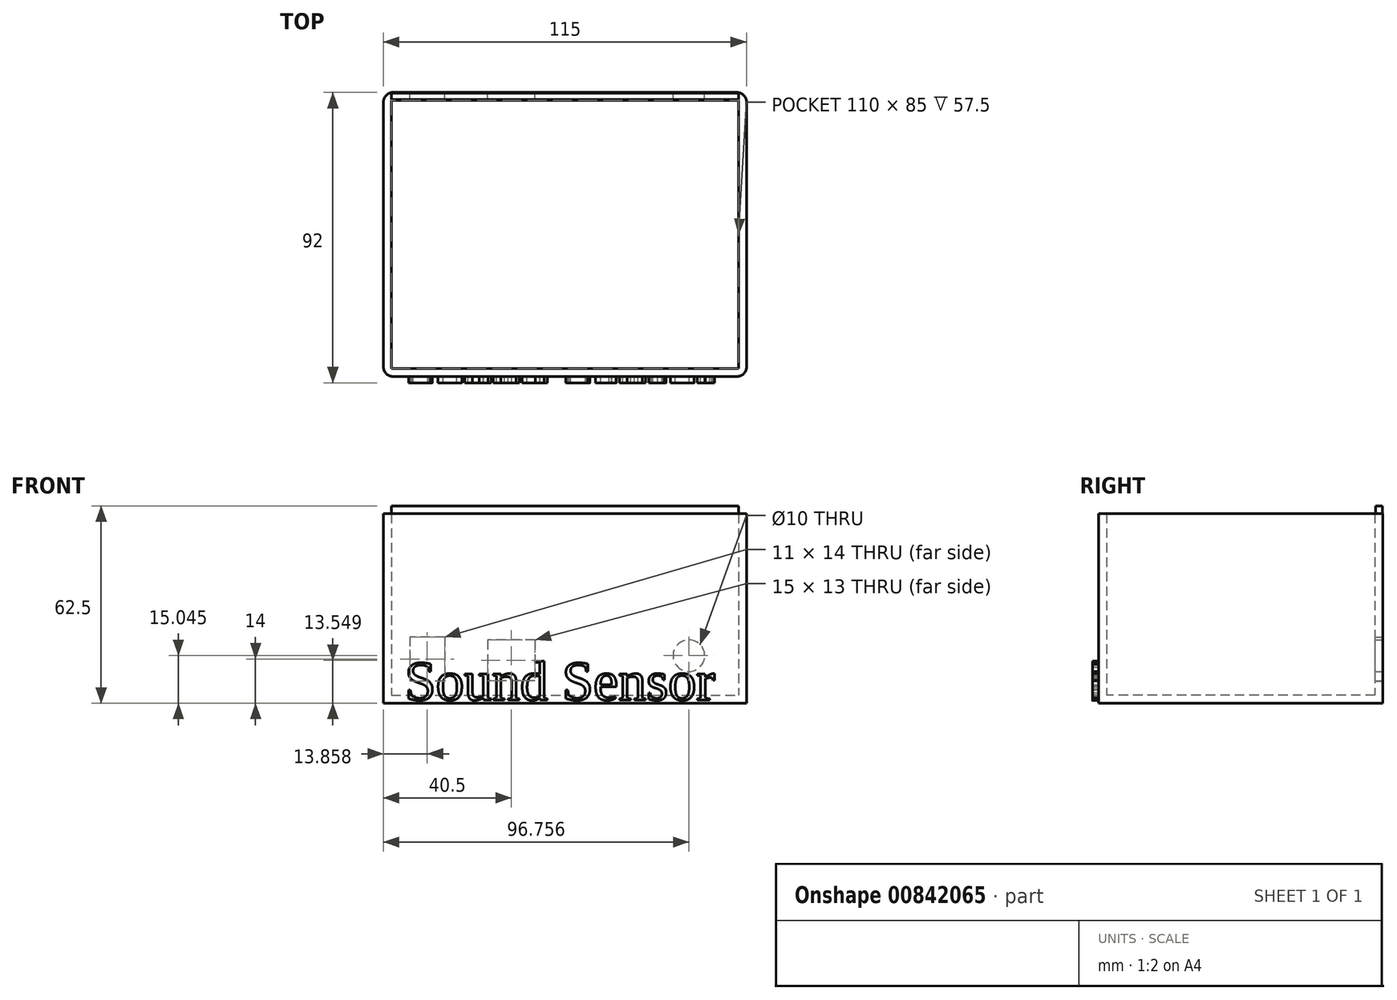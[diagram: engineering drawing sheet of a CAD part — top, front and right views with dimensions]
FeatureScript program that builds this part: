
annotation { "Feature Type Name" : "Feature", "Feature Type Description" : "" }
export const myFeature = defineFeature(function(context is Context, id is Id, definition is map)
    precondition{}
    {
        {
            var Q0;
            Q0=qCreatedBy(makeId("Top.planeOp"),FACE);
            var sketch = newSketch(context, id + "F0", { "sketchPlane" : qUnion([Q0])});
            skLineSegment(sketch, "E0.bottom", {"start": v(-57.5, 43.87) * mm, "end": v(57.5, 43.87) * mm});
            skLineSegment(sketch, "E0.top", {"start": v(-57.5, -46.13) * mm, "end": v(57.5, -46.13) * mm});
            skLineSegment(sketch, "E0.left", {"start": v(-57.5, 43.87) * mm, "end": v(-57.5, -46.13) * mm});
            skLineSegment(sketch, "E0.right", {"start": v(57.5, 43.87) * mm, "end": v(57.5, -46.13) * mm});
            skLineSegment(sketch, "E1", {"start": v(0, 29.34) * mm, "end": v(57.5, 29.34) * mm});
            skSolve(sketch);
        }
        {
            var Q0;
            Q0=qSketchRegion(id+"F0",true);
            extrude(context, id + "F1", {"entities" : qUnion([Q0]), "depth" : 60 * mm, "offsetDistance" : 25 * mm});
        }
        {
            var Q0;
            Q0=makeQuery(id+"F1.opExtrude","CAP_FACE",FACE,{"disambiguationData":[OSD([sQuery(id+"F0.wireOp",EDGE,"E0.bottom"),sQuery(id+"F0.wireOp",EDGE,"E0.top"),sQuery(id+"F0.wireOp",EDGE,"E0.left"),sQuery(id+"F0.wireOp",EDGE,"E0.right")])],"isStart":false});
            shell(context, id + "F2", {"entities" : qUnion([Q0]), "thickness" : 2.5 * mm});
        }
        {
            var Q0;
            Q0=makeQuery(id+"F1.opExtrude","SWEPT_FACE",FACE,{"disambiguationData":[OSD([sQuery(id+"F0.wireOp",EDGE,"E0.bottom")])]});
            var sketch = newSketch(context, id + "F3", { "sketchPlane" : qUnion([Q0])});
            skLineSegment(sketch, "E2.bottom", {"start": v(9.5, 20.05) * mm, "end": v(24.5, 20.05) * mm});
            skLineSegment(sketch, "E2.top", {"start": v(9.5, 7.05) * mm, "end": v(24.5, 7.05) * mm});
            skLineSegment(sketch, "E2.left", {"start": v(9.5, 20.05) * mm, "end": v(9.5, 7.05) * mm});
            skLineSegment(sketch, "E2.right", {"start": v(24.5, 20.05) * mm, "end": v(24.5, 7.05) * mm});
            skLineSegment(sketch, "E3.bottom", {"start": v(38.14, 21) * mm, "end": v(49.14, 21) * mm});
            skLineSegment(sketch, "E3.top", {"start": v(38.14, 7) * mm, "end": v(49.14, 7) * mm});
            skLineSegment(sketch, "E3.left", {"start": v(38.14, 21) * mm, "end": v(38.14, 7) * mm});
            skLineSegment(sketch, "E3.right", {"start": v(49.14, 21) * mm, "end": v(49.14, 7) * mm});
            skLineSegment(sketch, "E4", {"start": v(49.14, 7) * mm, "end": v(55.14, 7) * mm});
            skLineSegment(sketch, "E5", {"start": v(52.22, 7) * mm, "end": v(52.22, 0) * mm});
            skLineSegment(sketch, "E6", {"start": v(9.5, -6.68) * mm, "end": v(57.5, -6.68) * mm});
            skLineSegment(sketch, "E7", {"start": v(57.5, 0) * mm, "end": v(57.5, -11.21) * mm});
            skLineSegment(sketch, "E8", {"start": v(24.5, 17.96) * mm, "end": v(38.14, 17.96) * mm});
            skCircle(sketch, "E9", {"center": v(-39.26, 15.04) * mm, "radius": 5 * mm});
            skSolve(sketch);
        }
        {
            var Q0;
            Q0=qSketchRegion(id+"F3",true);
            extrude(context, id + "F4", {"entities" : qUnion([Q0]), "operationType" : NewBodyOperationType.REMOVE, "oppositeDirection" : true, "depth" : 2.5 * mm, "offsetDistance" : 25 * mm});
        }
        {
            var Q0;
            Q0=makeQuery(id+"F1.opExtrude","SWEPT_EDGE",EDGE,{"disambiguationData":[OSD([sQuery(id+"F0.wireOp",EDGE,"E0.top"),sQuery(id+"F0.wireOp",EDGE,"E0.right")])]});
            var Q1;
            Q1=makeQuery(id+"F1.opExtrude","SWEPT_EDGE",EDGE,{"disambiguationData":[OSD([sQuery(id+"F0.wireOp",EDGE,"E0.top"),sQuery(id+"F0.wireOp",EDGE,"E0.left")])]});
            var Q2;
            Q2=makeQuery(id+"F1.opExtrude","SWEPT_EDGE",EDGE,{"disambiguationData":[OSD([sQuery(id+"F0.wireOp",EDGE,"E0.bottom"),sQuery(id+"F0.wireOp",EDGE,"E0.left")])]});
            var Q3;
            Q3=makeQuery(id+"F1.opExtrude","SWEPT_EDGE",EDGE,{"disambiguationData":[OSD([sQuery(id+"F0.wireOp",EDGE,"E0.bottom"),sQuery(id+"F0.wireOp",EDGE,"E0.right")])]});
            fillet(context, id + "F5", {"entities" : qUnion([Q0, Q1, Q2, Q3]), "radius" : 3 * mm, "tangentPropagation" : true, "allowEdgeOverflow" : false});
        }
        {
            var Q0;
            Q0=makeQuery(id+"F1.opExtrude","SWEPT_FACE",FACE,{"disambiguationData":[OSD([sQuery(id+"F0.wireOp",EDGE,"E0.top")])]});
            var sketch = newSketch(context, id + "F6", { "sketchPlane" : qUnion([Q0])});
            skText(sketch, "E10", { "text": "Sound Sensor", "fontName": "Tinos-Regular.ttf"});
            const initialGuessF6  = {"E10": [-0.05076, 0.00104, 1, 0, 0.0128]};
            skSetInitialGuess(sketch, initialGuessF6);
            skSolve(sketch);
        }
        {
            var Q0;
            Q0=qSketchRegion(id+"F6",true);
            extrude(context, id + "F7", {"entities" : qUnion([Q0]), "operationType" : NewBodyOperationType.ADD, "depth" : 2 * mm, "offsetDistance" : 25 * mm});
        }
        {
            var Q0;
            Q0=qCreatedBy(makeId("Right.planeOp"),FACE);
            var sketch = newSketch(context, id + "F8", { "sketchPlane" : qUnion([Q0])});
            skLineSegment(sketch, "E11", {"start": v(43.87, 60) * mm, "end": v(43.67, 60) * mm});
            skLineSegment(sketch, "E12", {"start": v(41.77, 59.76) * mm, "end": v(41.97, 59.76) * mm});
            skLineSegment(sketch, "E13.bottom", {"start": v(43.67, 62.5) * mm, "end": v(41.57, 62.5) * mm});
            skLineSegment(sketch, "E13.top", {"start": v(43.67, 60) * mm, "end": v(41.57, 60) * mm});
            skLineSegment(sketch, "E13.left", {"start": v(43.67, 62.5) * mm, "end": v(43.67, 60) * mm});
            skLineSegment(sketch, "E13.right", {"start": v(41.57, 62.5) * mm, "end": v(41.57, 60) * mm});
            skSolve(sketch);
        }
        {
            var Q0;
            Q0=makeQuery(id+"F8.imprint","IMPRINT",FACE,{"disambiguationData":[TD([[makeQuery(id+"F8.imprint","IMPRINT",EDGE,{"derivedFrom":sQuery(id+"F8.wireOp",EDGE,"Zby9UUfq-n1uA-eyAV-TH90-8IeheHpzIfhT.bottom")}),1.0]])]});
            var Q1;
            Q1=makeQuery(id+"F8.imprint","IMPRINT",FACE,{"disambiguationData":[TD([[makeQuery(id+"F8.imprint","IMPRINT",EDGE,{"derivedFrom":sQuery(id+"F8.wireOp",EDGE,"E13.bottom")}),1.0]])]});
            extrude(context, id + "F9", {"entities" : qUnion([Q0, Q1]), "oppositeDirection" : true, "depth" : 110 * mm, "offsetDistance" : 25 * mm, "symmetric" : true});
        }
    });
